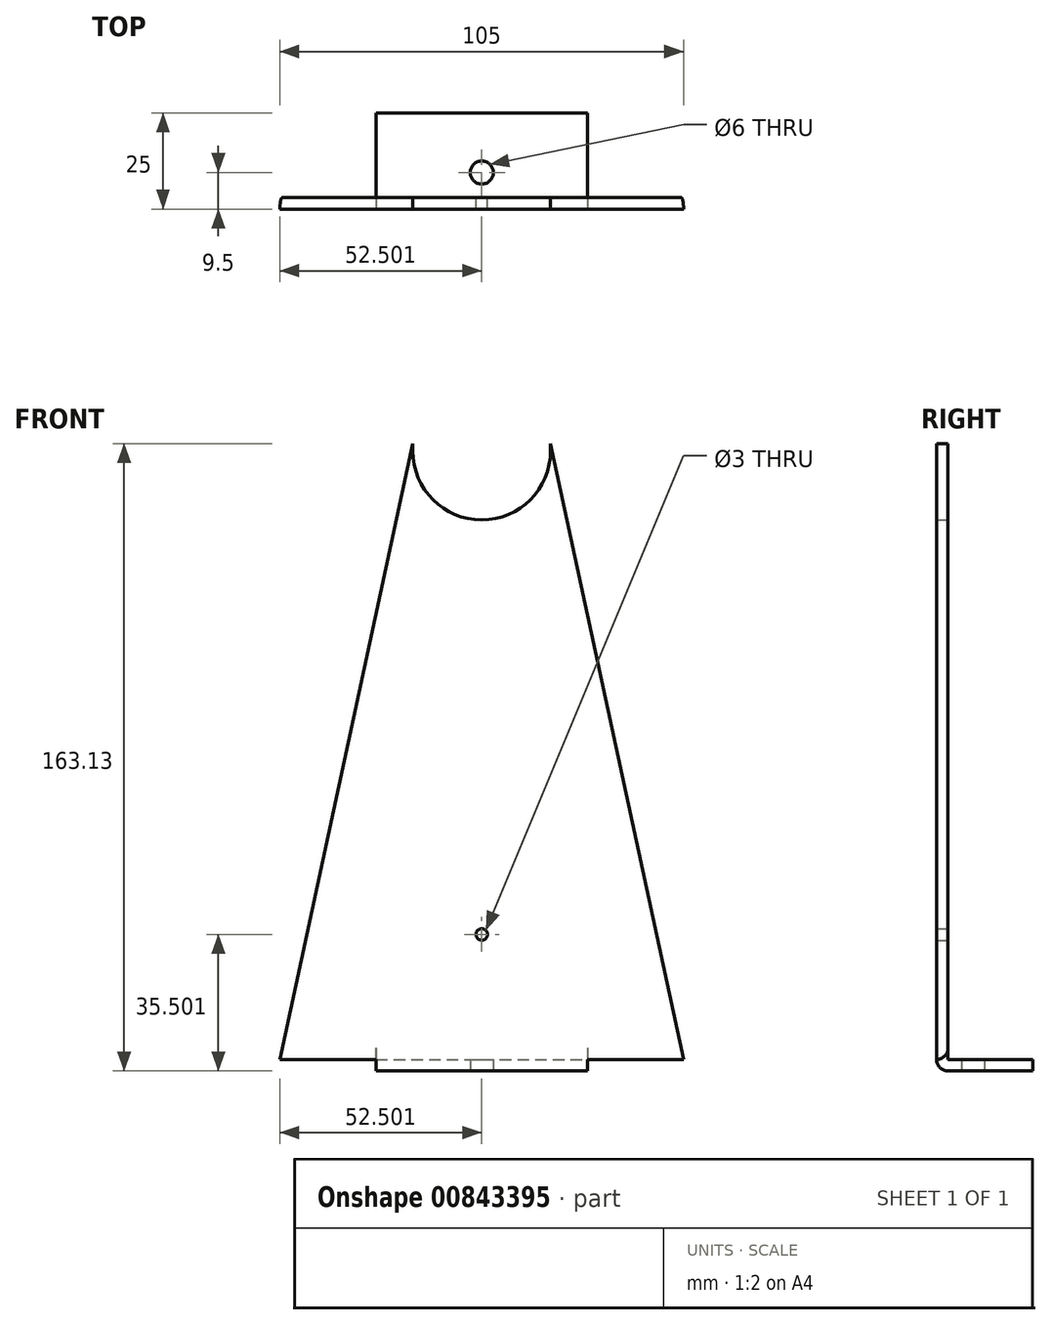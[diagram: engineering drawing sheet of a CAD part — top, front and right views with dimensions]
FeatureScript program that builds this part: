
annotation { "Feature Type Name" : "Feature", "Feature Type Description" : "" }
export const myFeature = defineFeature(function(context is Context, id is Id, definition is map)
    precondition{}
    {
        {
            var Q0;
            Q0=qCreatedBy(makeId("Front.planeOp"),FACE);
            var sketch = newSketch(context, id + "F0", { "sketchPlane" : qUnion([Q0])});
            skCircle(sketch, "E0", {"center": v(1053.9, -134.2) * mm, "radius": 17 * mm, "construction": true});
            skLineSegment(sketch, "E1", {"start": v(1680.14, -90.33) * mm, "end": v(1488.5, 408.9) * mm, "construction": true});
            skCircle(sketch, "E2", {"center": v(1053.9, -134.2) * mm, "radius": 21.5 * mm, "construction": true});
            skLineSegment(sketch, "E3", {"start": v(600.85, -74.2) * mm, "end": v(1722.15, -74.2) * mm, "construction": true});
            skLineSegment(sketch, "E4", {"start": v(549.42, 30.42) * mm, "end": v(557.61, 24.68) * mm, "construction": true});
            skLineSegment(sketch, "E5", {"start": v(556.15, 25.16) * mm, "end": v(512.34, -39.07) * mm, "construction": true});
            skLineSegment(sketch, "E6", {"start": v(553.17, 27) * mm, "end": v(509.45, -37.1) * mm, "construction": true});
            skLineSegment(sketch, "E7", {"start": v(550.2, 28.85) * mm, "end": v(506.56, -35.12) * mm, "construction": true});
            skLineSegment(sketch, "E8", {"start": v(506.6, -35.05) * mm, "end": v(512.39, -39) * mm, "construction": true});
            skLineSegment(sketch, "E9", {"start": v(570.93, 38.38) * mm, "end": v(557.61, 24.68) * mm, "construction": true});
            skLineSegment(sketch, "E10", {"start": v(552.29, 40.23) * mm, "end": v(549.42, 30.42) * mm, "construction": true});
            skLineSegment(sketch, "E11", {"start": v(600.85, -74.2) * mm, "end": v(440.53, 35.16) * mm, "construction": true});
            skLineSegment(sketch, "E12", {"start": v(713.05, 305.42) * mm, "end": v(656.4, 344.07) * mm, "construction": true});
            skLineSegment(sketch, "E13", {"start": v(702.52, 301.1) * mm, "end": v(656.02, 332.82) * mm, "construction": true});
            skLineSegment(sketch, "E14", {"start": v(710.06, 318.96) * mm, "end": v(669.92, 346.34) * mm, "construction": true});
            skLineSegment(sketch, "E15", {"start": v(689.46, 276.92) * mm, "end": v(655.21, 300.28) * mm, "construction": true});
            skLineSegment(sketch, "E16", {"start": v(615.02, -14.4) * mm, "end": v(402.92, 130.27) * mm, "construction": true});
            skLineSegment(sketch, "E17", {"start": v(559.84, 45.15) * mm, "end": v(550.25, 28.9) * mm, "construction": true});
            skLineSegment(sketch, "E18", {"start": v(562.86, 43.37) * mm, "end": v(553.2, 26.99) * mm, "construction": true});
            skLineSegment(sketch, "E19", {"start": v(565.87, 41.59) * mm, "end": v(556.13, 25.08) * mm, "construction": true});
            skLineSegment(sketch, "E20", {"start": v(565.87, 41.59) * mm, "end": v(559.84, 45.15) * mm, "construction": true});
            skLineSegment(sketch, "E21", {"start": v(472.04, 13.66) * mm, "end": v(769.02, 448.32) * mm, "construction": true});
            skArc(sketch, "E22", {"start": v(1006.96, -304.39) * mm, "mid": v(1011.65, -296.38) * mm, "end": v(1009.48, -287.35) * mm, "construction": true});
            skLineSegment(sketch, "E23", {"start": v(1053.9, -134.2) * mm, "end": v(1026.77, -317.41) * mm, "construction": true});
            skLineSegment(sketch, "E24", {"start": v(919.77, -241.35) * mm, "end": v(912.74, -288.83) * mm, "construction": true});
            skLineSegment(sketch, "E25", {"start": v(652.5, -164.98) * mm, "end": v(650.65, -171.73) * mm, "construction": true});
            skLineSegment(sketch, "E26", {"start": v(1031.93, -282.2) * mm, "end": v(579.95, -215.37) * mm, "construction": true});
            skLineSegment(sketch, "E27", {"start": v(674.61, -285.96) * mm, "end": v(640.98, -281) * mm, "construction": true});
            skLineSegment(sketch, "E28", {"start": v(675.34, -281.02) * mm, "end": v(641.71, -276.04) * mm, "construction": true});
            skLineSegment(sketch, "E29", {"start": v(1058.23, -251.72) * mm, "end": v(1048.27, -318.98) * mm, "construction": true});
            skLineSegment(sketch, "E30", {"start": v(945.2, -240.52) * mm, "end": v(983.81, -252.86) * mm, "construction": true});
            skLineSegment(sketch, "E31", {"start": v(941.1, -296.9) * mm, "end": v(949.25, -241.81) * mm, "construction": true});
            skLineSegment(sketch, "E32", {"start": v(941.66, -296.89) * mm, "end": v(949.79, -241.98) * mm, "construction": true});
            skLineSegment(sketch, "E33", {"start": v(973.82, -296.4) * mm, "end": v(980.43, -251.78) * mm, "construction": true});
            skLineSegment(sketch, "E34", {"start": v(972.56, -296.41) * mm, "end": v(979.23, -251.4) * mm, "construction": true});
            skLineSegment(sketch, "E35", {"start": v(964.98, -243.46) * mm, "end": v(956.63, -299.87) * mm, "construction": true});
            skLineSegment(sketch, "E36", {"start": v(983.81, -252.86) * mm, "end": v(977.37, -296.34) * mm, "construction": true});
            skLineSegment(sketch, "E37", {"start": v(945.2, -240.52) * mm, "end": v(936.84, -296.96) * mm, "construction": true});
            skLineSegment(sketch, "E38", {"start": v(979.95, -251.62) * mm, "end": v(973.32, -296.4) * mm, "construction": true});
            skLineSegment(sketch, "E39", {"start": v(949.06, -241.75) * mm, "end": v(940.9, -296.9) * mm, "construction": true});
            skLineSegment(sketch, "E40", {"start": v(940.66, -271.21) * mm, "end": v(945.36, -271.9) * mm, "construction": true});
            skLineSegment(sketch, "E41", {"start": v(944.62, -276.85) * mm, "end": v(939.93, -276.16) * mm, "construction": true});
            skLineSegment(sketch, "E42", {"start": v(946.27, -261.93) * mm, "end": v(942.12, -261.32) * mm, "construction": true});
            skLineSegment(sketch, "E43", {"start": v(940.8, -270.22) * mm, "end": v(945.5, -270.92) * mm, "construction": true});
            skLineSegment(sketch, "E44", {"start": v(941.39, -266.26) * mm, "end": v(946.09, -266.96) * mm, "construction": true});
            skLineSegment(sketch, "E45", {"start": v(941.24, -267.25) * mm, "end": v(945.94, -267.95) * mm, "construction": true});
            skArc(sketch, "E46", {"start": v(960.04, -276.86) * mm, "mid": v(966, -272.44) * mm, "end": v(961.58, -266.47) * mm, "construction": true});
            skArc(sketch, "E47", {"start": v(961.58, -266.47) * mm, "mid": v(955.61, -270.9) * mm, "end": v(960.04, -276.86) * mm, "construction": true});
            skLineSegment(sketch, "E48", {"start": v(1015.7, -245.42) * mm, "end": v(1005.73, -312.69) * mm, "construction": true});
            skLineSegment(sketch, "E49", {"start": v(1048.27, -318.98) * mm, "end": v(1005.73, -312.69) * mm, "construction": true});
            skLineSegment(sketch, "E50", {"start": v(1058.23, -251.72) * mm, "end": v(1015.7, -245.42) * mm, "construction": true});
            skArc(sketch, "E51", {"start": v(1011.94, -270.77) * mm, "mid": v(1016.63, -262.76) * mm, "end": v(1014.46, -253.73) * mm, "construction": true});
            skLineSegment(sketch, "E52", {"start": v(1037.98, -241.64) * mm, "end": v(948.95, -228.46) * mm, "construction": true});
            skLineSegment(sketch, "E53", {"start": v(576.43, -151.16) * mm, "end": v(632.5, -159.46) * mm, "construction": true});
            skLineSegment(sketch, "E54", {"start": v(575.4, -158.08) * mm, "end": v(631.06, -166.32) * mm, "construction": true});
            skLineSegment(sketch, "E55", {"start": v(575.3, -152) * mm, "end": v(574.56, -156.95) * mm, "construction": true});
            skArc(sketch, "E56", {"start": v(574.56, -156.95) * mm, "mid": v(574.75, -157.7) * mm, "end": v(575.4, -158.08) * mm, "construction": true});
            skArc(sketch, "E57", {"start": v(576.43, -151.16) * mm, "mid": v(575.69, -151.35) * mm, "end": v(575.3, -152) * mm, "construction": true});
            skLineSegment(sketch, "E58", {"start": v(631.06, -166.32) * mm, "end": v(650.65, -171.73) * mm, "construction": true});
            skLineSegment(sketch, "E59", {"start": v(632.5, -159.46) * mm, "end": v(652.5, -164.98) * mm, "construction": true});
            skLineSegment(sketch, "E60", {"start": v(600.85, -74.2) * mm, "end": v(567.5, -299.5) * mm, "construction": true});
            skLineSegment(sketch, "E61", {"start": v(644.77, -80.7) * mm, "end": v(612.1, -301.34) * mm, "construction": true});
            skLineSegment(sketch, "E62", {"start": v(641.71, -276.04) * mm, "end": v(640.98, -281) * mm, "construction": true});
            skLineSegment(sketch, "E63", {"start": v(675.34, -281.02) * mm, "end": v(674.61, -285.96) * mm, "construction": true});
            skLineSegment(sketch, "E64", {"start": v(607.36, -8.75) * mm, "end": v(864.68, 368.48) * mm, "construction": true});
            skLineSegment(sketch, "E65", {"start": v(622.48, -20.32) * mm, "end": v(871.92, 345.36) * mm, "construction": true});
            skLineSegment(sketch, "E66", {"start": v(615.02, -14.4) * mm, "end": v(879.24, 372.95) * mm, "construction": true});
            skLineSegment(sketch, "E67", {"start": v(1053.9, -134.2) * mm, "end": v(865.03, 414.2) * mm, "construction": true});
            skLineSegment(sketch, "E68", {"start": v(1034.15, -125.7) * mm, "end": v(850, 409.01) * mm, "construction": true});
            skLineSegment(sketch, "E69", {"start": v(861.66, 381.3) * mm, "end": v(851.9, 409.67) * mm, "construction": true});
            skLineSegment(sketch, "E70", {"start": v(1064.21, -115.34) * mm, "end": v(880.07, 419.37) * mm, "construction": true});
            skLineSegment(sketch, "E71", {"start": v(1053.9, -134.2) * mm, "end": v(645.8, -73.78) * mm, "construction": true});
            skLineSegment(sketch, "E72", {"start": v(743.09, -99.4) * mm, "end": v(644.17, -84.76) * mm, "construction": true});
            skLineSegment(sketch, "E73", {"start": v(746.34, -77.44) * mm, "end": v(647.42, -62.8) * mm, "construction": true});
            skLineSegment(sketch, "E74", {"start": v(1035.36, -145.1) * mm, "end": v(841.66, -116.43) * mm, "construction": true});
            skLineSegment(sketch, "E75", {"start": v(1039.32, -118.4) * mm, "end": v(845.61, -89.72) * mm, "construction": true});
            skLineSegment(sketch, "E76", {"start": v(879.24, 372.95) * mm, "end": v(768.93, 448.19) * mm, "construction": true});
            skLineSegment(sketch, "E77", {"start": v(966.15, -134.86) * mm, "end": v(995.58, -139.21) * mm, "construction": true});
            skLineSegment(sketch, "E78", {"start": v(960.23, -139.03) * mm, "end": v(994.85, -144.16) * mm, "construction": true});
            skLineSegment(sketch, "E79", {"start": v(963.6, -143.58) * mm, "end": v(964.04, -140.6) * mm, "construction": true});
            skArc(sketch, "E80", {"start": v(959.64, -143) * mm, "mid": v(959.83, -143.73) * mm, "end": v(960.48, -144.13) * mm, "construction": true});
            skLineSegment(sketch, "E81", {"start": v(960.48, -144.13) * mm, "end": v(962.46, -144.42) * mm, "construction": true});
            skArc(sketch, "E82", {"start": v(962.46, -144.42) * mm, "mid": v(963.2, -144.23) * mm, "end": v(963.6, -143.58) * mm, "construction": true});
            skLineSegment(sketch, "E83", {"start": v(965.3, -133.72) * mm, "end": v(967.21, -120.86) * mm, "construction": true});
            skLineSegment(sketch, "E84", {"start": v(963, -120.24) * mm, "end": v(959.64, -143) * mm, "construction": true});
            skLineSegment(sketch, "E85", {"start": v(962.42, -124.2) * mm, "end": v(966.63, -124.82) * mm, "construction": true});
            skArc(sketch, "E86", {"start": v(965.17, -139.77) * mm, "mid": v(964.43, -139.95) * mm, "end": v(964.04, -140.6) * mm, "construction": true});
            skLineSegment(sketch, "E87", {"start": v(961.7, -129.14) * mm, "end": v(965.9, -129.76) * mm, "construction": true});
            skLineSegment(sketch, "E88", {"start": v(960.08, -126.38) * mm, "end": v(968.24, -127.58) * mm, "construction": true});
            skLineSegment(sketch, "E89", {"start": v(974.82, -141.2) * mm, "end": v(975.55, -136.25) * mm, "construction": true});
            skArc(sketch, "E90", {"start": v(965.3, -133.72) * mm, "mid": v(965.5, -134.46) * mm, "end": v(966.15, -134.86) * mm, "construction": true});
            skLineSegment(sketch, "E91", {"start": v(964.14, -119.4) * mm, "end": v(966.37, -119.73) * mm, "construction": true});
            skArc(sketch, "E92", {"start": v(964.14, -119.4) * mm, "mid": v(963.4, -119.58) * mm, "end": v(963, -120.24) * mm, "construction": true});
            skArc(sketch, "E93", {"start": v(967.21, -120.86) * mm, "mid": v(967.03, -120.12) * mm, "end": v(966.37, -119.73) * mm, "construction": true});
            skLineSegment(sketch, "E94", {"start": v(995.58, -139.21) * mm, "end": v(999.8, -144.9) * mm, "construction": true});
            skLineSegment(sketch, "E95", {"start": v(979.72, -143.94) * mm, "end": v(981.04, -135.04) * mm, "construction": true});
            skArc(sketch, "E96", {"start": v(995.7, -145.3) * mm, "mid": v(995.5, -144.55) * mm, "end": v(994.85, -144.16) * mm, "construction": true});
            skArc(sketch, "E97", {"start": v(995.25, -148.26) * mm, "mid": v(995.44, -149) * mm, "end": v(996.1, -149.4) * mm, "construction": true});
            skArc(sketch, "E98", {"start": v(998.07, -149.7) * mm, "mid": v(998.82, -149.5) * mm, "end": v(999.2, -148.85) * mm, "construction": true});
            skLineSegment(sketch, "E99", {"start": v(996.1, -149.4) * mm, "end": v(998.07, -149.7) * mm, "construction": true});
            skLineSegment(sketch, "E100", {"start": v(999.2, -148.85) * mm, "end": v(999.8, -144.9) * mm, "construction": true});
            skLineSegment(sketch, "E101", {"start": v(995.25, -148.26) * mm, "end": v(995.7, -145.3) * mm, "construction": true});
            skLineSegment(sketch, "E102", {"start": v(985.2, -142.73) * mm, "end": v(985.94, -137.79) * mm, "construction": true});
            skLineSegment(sketch, "E103", {"start": v(995.47, -146.78) * mm, "end": v(993.6, -159.38) * mm, "construction": true});
            skEllipticalArc(sketch, "E104", {"construction": true});
            skLineSegment(sketch, "E105", {"start": v(850, 409.01) * mm, "end": v(880.07, 419.37) * mm, "construction": true});
            skLineSegment(sketch, "E106", {"start": v(859.77, 380.65) * mm, "end": v(861.66, 381.3) * mm, "construction": true});
            skLineSegment(sketch, "E107", {"start": v(1053.92, -134.2) * mm, "end": v(1520.05, 326.73) * mm, "construction": true});
            skLineSegment(sketch, "E108", {"start": v(1075.4, -135.33) * mm, "end": v(1510.36, 294.78) * mm, "construction": true});
            skLineSegment(sketch, "E109", {"start": v(1060.7, -105.14) * mm, "end": v(1497.91, 327.2) * mm, "construction": true});
            skLineSegment(sketch, "E110", {"start": v(879.24, 372.95) * mm, "end": v(1502.3, 372.95) * mm, "construction": true});
            skLineSegment(sketch, "E111", {"start": v(901.53, 357.05) * mm, "end": v(1486.45, 357.05) * mm, "construction": true});
            skLineSegment(sketch, "E112", {"start": v(890.58, 388.85) * mm, "end": v(1474.25, 388.85) * mm, "construction": true});
            skArc(sketch, "E113", {"start": v(1486.5, 356.93) * mm, "mid": v(1487.54, 375.64) * mm, "end": v(1474.25, 388.85) * mm, "construction": true});
            skArc(sketch, "E114", {"start": v(890.58, 388.85) * mm, "mid": v(888.92, 370.5) * mm, "end": v(901.53, 357.05) * mm, "construction": true});
            skArc(sketch, "E115", {"start": v(1510.36, 294.78) * mm, "mid": v(1511.76, 313.92) * mm, "end": v(1497.91, 327.2) * mm, "construction": true});
            skLineSegment(sketch, "E116", {"start": v(1722.15, -74.2) * mm, "end": v(1680.14, -90.33) * mm, "construction": true});
            skLineSegment(sketch, "E117", {"start": v(915.6, -231.4) * mm, "end": v(630.6, -162.69) * mm, "construction": true});
            skLineSegment(sketch, "E118", {"start": v(913.6, -239.65) * mm, "end": v(801.39, -212.6) * mm, "construction": true});
            skLineSegment(sketch, "E119", {"start": v(917.6, -223.13) * mm, "end": v(805.37, -196.07) * mm, "construction": true});
            skArc(sketch, "E120", {"start": v(924, -233.74) * mm, "mid": v(919.82, -232.5) * mm, "end": v(915.6, -231.4) * mm, "construction": true});
            skArc(sketch, "E121", {"start": v(921.8, -241.96) * mm, "mid": v(917.73, -240.73) * mm, "end": v(913.6, -239.65) * mm, "construction": true});
            skArc(sketch, "E122", {"start": v(919.09, -223.5) * mm, "mid": v(918.34, -223.31) * mm, "end": v(917.6, -223.13) * mm, "construction": true});
            skLineSegment(sketch, "E123", {"start": v(631.26, -168.55) * mm, "end": v(633.85, -157.83) * mm, "construction": true});
            skLineSegment(sketch, "E124", {"start": v(1013.2, -262.25) * mm, "end": v(924, -233.74) * mm, "construction": true});
            skLineSegment(sketch, "E125", {"start": v(1011.94, -270.77) * mm, "end": v(921.42, -241.84) * mm, "construction": true});
            skLineSegment(sketch, "E126", {"start": v(1014.46, -253.73) * mm, "end": v(985.84, -244.58) * mm, "construction": true});
            skLineSegment(sketch, "E127", {"start": v(631.26, -168.55) * mm, "end": v(641.06, -174.4) * mm, "construction": true});
            skLineSegment(sketch, "E128", {"start": v(633.85, -157.83) * mm, "end": v(651.56, -156.6) * mm, "construction": true});
            skLineSegment(sketch, "E129", {"start": v(805.37, -196.07) * mm, "end": v(651.56, -156.6) * mm, "construction": true});
            skLineSegment(sketch, "E130", {"start": v(693.7, -188.3) * mm, "end": v(801.39, -212.6) * mm, "construction": true});
            skLineSegment(sketch, "E131", {"start": v(641.06, -174.4) * mm, "end": v(688.9, -185.2) * mm, "construction": true});
            skArc(sketch, "E132", {"start": v(905.87, -297.16) * mm, "mid": v(910.24, -297.33) * mm, "end": v(914.6, -297.34) * mm, "construction": true});
            skArc(sketch, "E133", {"start": v(906.36, -288.67) * mm, "mid": v(910.61, -288.83) * mm, "end": v(914.87, -288.83) * mm, "construction": true});
            skArc(sketch, "E134", {"start": v(905.39, -305.65) * mm, "mid": v(910.06, -305.83) * mm, "end": v(914.73, -305.84) * mm, "construction": true});
            skLineSegment(sketch, "E135", {"start": v(1008.18, -295.87) * mm, "end": v(914.6, -297.34) * mm, "construction": true});
            skLineSegment(sketch, "E136", {"start": v(1009.48, -287.35) * mm, "end": v(914.47, -288.84) * mm, "construction": true});
            skLineSegment(sketch, "E137", {"start": v(1006.96, -304.39) * mm, "end": v(914.73, -305.84) * mm, "construction": true});
            skLineSegment(sketch, "E138", {"start": v(688.9, -185.2) * mm, "end": v(693.7, -188.3) * mm, "construction": true});
            skArc(sketch, "E139", {"start": v(919.09, -223.5) * mm, "mid": v(951.5, -237.06) * mm, "end": v(985.84, -244.58) * mm, "construction": true});
            skLineSegment(sketch, "E140", {"start": v(936.85, -296.96) * mm, "end": v(977.38, -296.34) * mm, "construction": true});
            skFitSpline(sketch, "E141", {"points": [v(872.4, 346.08) * mm, v(876.18, 356.24) * mm, v(881.69, 371.02) * mm, v(868.73, 369.09) * mm, v(864.68, 368.48) * mm], "construction": true});
            skLineSegment(sketch, "E142", {"start": v(662.14, -86.28) * mm, "end": v(644.63, -83.68) * mm, "construction": true});
            skLineSegment(sketch, "E143", {"start": v(665.07, -66.5) * mm, "end": v(647.56, -63.9) * mm, "construction": true});
            skLineSegment(sketch, "E144", {"start": v(664.41, -84.6) * mm, "end": v(666.76, -68.76) * mm, "construction": true});
            skArc(sketch, "E145", {"start": v(662.14, -86.28) * mm, "mid": v(663.62, -85.9) * mm, "end": v(664.41, -84.6) * mm, "construction": true});
            skArc(sketch, "E146", {"start": v(666.76, -68.76) * mm, "mid": v(666.38, -67.28) * mm, "end": v(665.07, -66.5) * mm, "construction": true});
            skArc(sketch, "E147", {"start": v(591.11, -61.72) * mm, "mid": v(584.1, -63.16) * mm, "end": v(585.54, -70.17) * mm, "construction": true});
            skLineSegment(sketch, "E148", {"start": v(585.54, -70.17) * mm, "end": v(605.08, -83.05) * mm, "construction": true});
            skLineSegment(sketch, "E149", {"start": v(601.2, -91.02) * mm, "end": v(582.02, -84.5) * mm, "construction": true});
            skLineSegment(sketch, "E150", {"start": v(584.15, -63.19) * mm, "end": v(613.37, -82.46) * mm, "construction": true});
            skLineSegment(sketch, "E151", {"start": v(607.46, -8.63) * mm, "end": v(572.75, -54.03) * mm, "construction": true});
            skLineSegment(sketch, "E152", {"start": v(644.18, -84.66) * mm, "end": v(644.29, -83.94) * mm, "construction": true});
            skLineSegment(sketch, "E153", {"start": v(591.11, -61.72) * mm, "end": v(618.65, -79.88) * mm, "construction": true});
            skArc(sketch, "E154", {"start": v(618.65, -79.88) * mm, "mid": v(620.57, -80.9) * mm, "end": v(622.66, -81.47) * mm, "construction": true});
            skLineSegment(sketch, "E155", {"start": v(644.18, -84.66) * mm, "end": v(622.66, -81.47) * mm, "construction": true});
            skArc(sketch, "E156", {"start": v(644.63, -83.68) * mm, "mid": v(644.4, -83.74) * mm, "end": v(644.29, -83.94) * mm, "construction": true});
            skLineSegment(sketch, "E157", {"start": v(644.18, -84.66) * mm, "end": v(644.19, -84.63) * mm, "construction": true});
            skArc(sketch, "E158", {"start": v(601.2, -91.02) * mm, "mid": v(606.49, -88.67) * mm, "end": v(605.08, -83.05) * mm, "construction": true});
            skArc(sketch, "E159", {"start": v(617.78, -52.64) * mm, "mid": v(628.06, -58.54) * mm, "end": v(639.47, -61.73) * mm, "construction": true});
            skLineSegment(sketch, "E160", {"start": v(670.48, -77.43) * mm, "end": v(577.33, -63.64) * mm, "construction": true});
            skLineSegment(sketch, "E161", {"start": v(647.4, -62.9) * mm, "end": v(639.47, -61.73) * mm, "construction": true});
            skArc(sketch, "E162", {"start": v(647.3, -63.56) * mm, "mid": v(647.36, -63.78) * mm, "end": v(647.56, -63.9) * mm, "construction": true});
            skLineSegment(sketch, "E163", {"start": v(647.3, -63.56) * mm, "end": v(647.4, -62.9) * mm, "construction": true});
            skArc(sketch, "E164", {"start": v(614, -32.51) * mm, "mid": v(611.92, -43.32) * mm, "end": v(617.78, -52.64) * mm, "construction": true});
            skLineSegment(sketch, "E165", {"start": v(614, -32.51) * mm, "end": v(622.56, -20.17) * mm, "construction": true});
            skLineSegment(sketch, "E166", {"start": v(577.33, -63.64) * mm, "end": v(629.71, 4.8) * mm, "construction": true});
            skArc(sketch, "E167", {"start": v(598.7, -25.94) * mm, "mid": v(602.23, -29.14) * mm, "end": v(601.27, -24.48) * mm, "construction": true});
            skArc(sketch, "E168", {"start": v(572.75, -54.03) * mm, "mid": v(569.56, -71.65) * mm, "end": v(582.02, -84.5) * mm, "construction": true});
            skCircle(sketch, "E169", {"center": v(586.41, -46.03) * mm, "radius": 2 * mm, "construction": true});
            skArc(sketch, "E170", {"start": v(585.71, -43.63) * mm, "mid": v(585.82, -48.46) * mm, "end": v(588.14, -44.23) * mm, "construction": true});
            skArc(sketch, "E171", {"start": v(632.31, -4.97) * mm, "mid": v(632.7, -3.49) * mm, "end": v(631.94, -2.16) * mm, "construction": true});
            skLineSegment(sketch, "E172", {"start": v(608.84, -9.3) * mm, "end": v(619.6, 4.75) * mm, "construction": true});
            skLineSegment(sketch, "E173", {"start": v(621.55, -19.02) * mm, "end": v(632.31, -4.97) * mm, "construction": true});
            skLineSegment(sketch, "E174", {"start": v(607.46, -8.63) * mm, "end": v(608.42, -9.36) * mm, "construction": true});
            skArc(sketch, "E175", {"start": v(621.55, -19.02) * mm, "mid": v(621.5, -19.24) * mm, "end": v(621.6, -19.44) * mm, "construction": true});
            skLineSegment(sketch, "E176", {"start": v(621.6, -19.44) * mm, "end": v(622.56, -20.17) * mm, "construction": true});
            skCircle(sketch, "E177", {"center": v(601, -26.97) * mm, "radius": 2 * mm, "construction": true});
            skArc(sketch, "E178", {"start": v(608.42, -9.36) * mm, "mid": v(608.64, -9.42) * mm, "end": v(608.84, -9.3) * mm, "construction": true});
            skLineSegment(sketch, "E179", {"start": v(608.42, -9.36) * mm, "end": v(607.46, -8.63) * mm, "construction": true});
            skArc(sketch, "E180", {"start": v(622.4, 5.12) * mm, "mid": v(620.93, 5.52) * mm, "end": v(619.6, 4.75) * mm, "construction": true});
            skLineSegment(sketch, "E181", {"start": v(631.94, -2.16) * mm, "end": v(622.4, 5.12) * mm, "construction": true});
            skLineSegment(sketch, "E182", {"start": v(619.71, -24.29) * mm, "end": v(604.42, -12.6) * mm, "construction": true});
            skLineSegment(sketch, "E183", {"start": v(639.24, -83.93) * mm, "end": v(642.46, -62.17) * mm, "construction": true});
            skCircle(sketch, "E184", {"center": v(600.85, -74.2) * mm, "radius": 5 * mm, "construction": true});
            skLineSegment(sketch, "E185", {"start": v(621.6, -19.44) * mm, "end": v(608.42, -9.36) * mm, "construction": true});
            skLineSegment(sketch, "E186", {"start": v(644.29, -83.94) * mm, "end": v(647.3, -63.56) * mm, "construction": true});
            skLineSegment(sketch, "E187", {"start": v(841.66, -116.43) * mm, "end": v(743.09, -99.4) * mm, "construction": true});
            skLineSegment(sketch, "E188", {"start": v(746.34, -77.44) * mm, "end": v(845.61, -89.72) * mm, "construction": true});
            skEllipse(sketch, "E189", {"center": v(843.64, -103.07) * mm, "majorRadius": 13.5 * mm, "minorRadius": 8.5 * mm, "majorAxis": v(-0.15, -0.99), "construction": true});
            skCircle(sketch, "E190", {"center": v(645.8, -73.78) * mm, "radius": 11 * mm, "construction": true});
            skLineSegment(sketch, "E191", {"start": v(634.82, -284.6) * mm, "end": v(635, -277.6) * mm, "construction": true});
            skLineSegment(sketch, "E192", {"start": v(558, -275.8) * mm, "end": v(614.08, -284.09) * mm, "construction": true});
            skLineSegment(sketch, "E193", {"start": v(559.02, -268.88) * mm, "end": v(614.68, -277.1) * mm, "construction": true});
            skLineSegment(sketch, "E194", {"start": v(557.16, -274.67) * mm, "end": v(557.89, -269.73) * mm, "construction": true});
            skArc(sketch, "E195", {"start": v(559.02, -268.88) * mm, "mid": v(558.28, -269.07) * mm, "end": v(557.89, -269.73) * mm, "construction": true});
            skArc(sketch, "E196", {"start": v(557.16, -274.67) * mm, "mid": v(557.34, -275.42) * mm, "end": v(558, -275.8) * mm, "construction": true});
            skLineSegment(sketch, "E197", {"start": v(614.68, -277.1) * mm, "end": v(635, -277.6) * mm, "construction": true});
            skLineSegment(sketch, "E198", {"start": v(614.08, -284.09) * mm, "end": v(634.82, -284.6) * mm, "construction": true});
            skLineSegment(sketch, "E199", {"start": v(905.87, -297.16) * mm, "end": v(613.19, -280.45) * mm, "construction": true});
            skLineSegment(sketch, "E200", {"start": v(906.36, -288.67) * mm, "end": v(791.11, -282.1) * mm, "construction": true});
            skLineSegment(sketch, "E201", {"start": v(905.39, -305.65) * mm, "end": v(790.14, -299.07) * mm, "construction": true});
            skLineSegment(sketch, "E202", {"start": v(615.52, -275.03) * mm, "end": v(614.89, -286.04) * mm, "construction": true});
            skLineSegment(sketch, "E203", {"start": v(615.52, -275.03) * mm, "end": v(632.73, -270.73) * mm, "construction": true});
            skLineSegment(sketch, "E204", {"start": v(614.89, -286.04) * mm, "end": v(631.5, -292.34) * mm, "construction": true});
            skLineSegment(sketch, "E205", {"start": v(790.14, -299.07) * mm, "end": v(631.5, -292.34) * mm, "construction": true});
            skLineSegment(sketch, "E206", {"start": v(632.73, -270.73) * mm, "end": v(791.11, -282.1) * mm, "construction": true});
            skLineSegment(sketch, "E207", {"start": v(703.93, 282.77) * mm, "end": v(553.52, 27.55) * mm, "construction": true});
            skArc(sketch, "E208", {"start": v(703.93, 282.77) * mm, "mid": v(707.75, 289.77) * mm, "end": v(711.1, 297.02) * mm, "construction": true});
            skArc(sketch, "E209", {"start": v(695.75, 287.6) * mm, "mid": v(699.27, 294.04) * mm, "end": v(702.35, 300.71) * mm, "construction": true});
            skArc(sketch, "E210", {"start": v(712.12, 277.95) * mm, "mid": v(716.24, 285.5) * mm, "end": v(719.85, 293.32) * mm, "construction": true});
            skLineSegment(sketch, "E211", {"start": v(712.12, 277.95) * mm, "end": v(570.93, 38.38) * mm, "construction": true});
            skLineSegment(sketch, "E212", {"start": v(695.75, 287.6) * mm, "end": v(578.7, 88.99) * mm, "construction": true});
            skLineSegment(sketch, "E213", {"start": v(577.7, 83.34) * mm, "end": v(552.29, 40.23) * mm, "construction": true});
            skLineSegment(sketch, "E214", {"start": v(764.21, 422.8) * mm, "end": v(711.1, 297.02) * mm, "construction": true});
            skLineSegment(sketch, "E215", {"start": v(781.6, 439.55) * mm, "end": v(719.85, 293.32) * mm, "construction": true});
            skLineSegment(sketch, "E216", {"start": v(758.12, 432.79) * mm, "end": v(702.35, 300.71) * mm, "construction": true});
            skLineSegment(sketch, "E217", {"start": v(452.18, 96.19) * mm, "end": v(408.28, 32.03) * mm, "construction": true});
            skLineSegment(sketch, "E218", {"start": v(454.99, 94.09) * mm, "end": v(411.17, 30.06) * mm, "construction": true});
            skLineSegment(sketch, "E219", {"start": v(457.79, 91.98) * mm, "end": v(414.05, 28.08) * mm, "construction": true});
            skLineSegment(sketch, "E220", {"start": v(414.1, 28.15) * mm, "end": v(408.33, 32.1) * mm, "construction": true});
            skLineSegment(sketch, "E221", {"start": v(577.7, 83.34) * mm, "end": v(578.7, 88.99) * mm, "construction": true});
            skCircle(sketch, "E222", {"center": v(795.03, 249.5) * mm, "radius": 9.5 * mm, "construction": true});
            skLineSegment(sketch, "E223", {"start": v(789.96, 238.43) * mm, "end": v(790.5, 237.46) * mm, "construction": true});
            skLineSegment(sketch, "E224", {"start": v(796.05, 242.82) * mm, "end": v(795.76, 244.37) * mm, "construction": true});
            skLineSegment(sketch, "E225", {"start": v(789.82, 248.52) * mm, "end": v(790.17, 248.58) * mm, "construction": true});
            skLineSegment(sketch, "E226", {"start": v(796.02, 244.3) * mm, "end": v(789.82, 248.52) * mm, "construction": true});
            skLineSegment(sketch, "E227", {"start": v(784, 242.2) * mm, "end": v(792.26, 236.56) * mm, "construction": true});
            skLineSegment(sketch, "E228", {"start": v(792.26, 236.56) * mm, "end": v(793.8, 238.84) * mm, "construction": true});
            skLineSegment(sketch, "E229", {"start": v(791.91, 236.5) * mm, "end": v(792.26, 236.56) * mm, "construction": true});
            skLineSegment(sketch, "E230", {"start": v(784.06, 241.85) * mm, "end": v(784, 242.2) * mm, "construction": true});
            skLineSegment(sketch, "E231", {"start": v(795.95, 244.64) * mm, "end": v(790.17, 248.58) * mm, "construction": true});
            skLineSegment(sketch, "E232", {"start": v(786.57, 240.74) * mm, "end": v(789.96, 238.43) * mm, "construction": true});
            skLineSegment(sketch, "E233", {"start": v(791.91, 236.5) * mm, "end": v(784.06, 241.85) * mm, "construction": true});
            skLineSegment(sketch, "E234", {"start": v(786.58, 243.77) * mm, "end": v(789.82, 248.52) * mm, "construction": true});
            skLineSegment(sketch, "E235", {"start": v(787.99, 239.18) * mm, "end": v(793.06, 246.61) * mm, "construction": true});
            skLineSegment(sketch, "E236", {"start": v(786.39, 240.48) * mm, "end": v(791.18, 247.5) * mm, "construction": true});
            skLineSegment(sketch, "E237", {"start": v(786.08, 240.81) * mm, "end": v(791, 248.02) * mm, "construction": true});
            skLineSegment(sketch, "E238", {"start": v(786.57, 240.74) * mm, "end": v(785.47, 240.9) * mm, "construction": true});
            skLineSegment(sketch, "E239", {"start": v(789.96, 238.43) * mm, "end": v(794.75, 245.46) * mm, "construction": true});
            skLineSegment(sketch, "E240", {"start": v(790.2, 238) * mm, "end": v(795.12, 245.2) * mm, "construction": true});
            skLineSegment(sketch, "E241", {"start": v(784, 242.2) * mm, "end": v(785.55, 244.47) * mm, "construction": true});
            skLineSegment(sketch, "E242", {"start": v(793.8, 238.84) * mm, "end": v(785.55, 244.47) * mm, "construction": true});
            skLineSegment(sketch, "E243", {"start": v(792.78, 239.54) * mm, "end": v(796.02, 244.3) * mm, "construction": true});
            skArc(sketch, "E244", {"start": v(962.06, -126.67) * mm, "mid": v(930.44, 82.62) * mm, "end": v(787.99, 239.18) * mm, "construction": true});
            skLineSegment(sketch, "E245", {"start": v(679.65, 313.68) * mm, "end": v(680.2, 312.7) * mm, "construction": true});
            skLineSegment(sketch, "E246", {"start": v(685.7, 319.54) * mm, "end": v(685.64, 319.88) * mm, "construction": true});
            skLineSegment(sketch, "E247", {"start": v(679.5, 323.76) * mm, "end": v(679.86, 323.83) * mm, "construction": true});
            skLineSegment(sketch, "E248", {"start": v(685.7, 319.54) * mm, "end": v(679.5, 323.76) * mm, "construction": true});
            skLineSegment(sketch, "E249", {"start": v(673.69, 317.44) * mm, "end": v(681.95, 311.8) * mm, "construction": true});
            skLineSegment(sketch, "E250", {"start": v(681.95, 311.8) * mm, "end": v(683.5, 314.08) * mm, "construction": true});
            skLineSegment(sketch, "E251", {"start": v(681.6, 311.74) * mm, "end": v(681.95, 311.8) * mm, "construction": true});
            skLineSegment(sketch, "E252", {"start": v(673.75, 317.1) * mm, "end": v(673.69, 317.44) * mm, "construction": true});
            skLineSegment(sketch, "E253", {"start": v(685.64, 319.88) * mm, "end": v(679.86, 323.83) * mm, "construction": true});
            skLineSegment(sketch, "E254", {"start": v(676.27, 315.99) * mm, "end": v(679.65, 313.68) * mm, "construction": true});
            skLineSegment(sketch, "E255", {"start": v(681.6, 311.74) * mm, "end": v(673.75, 317.1) * mm, "construction": true});
            skLineSegment(sketch, "E256", {"start": v(676.27, 319.01) * mm, "end": v(679.5, 323.76) * mm, "construction": true});
            skLineSegment(sketch, "E257", {"start": v(677.68, 314.42) * mm, "end": v(682.75, 321.86) * mm, "construction": true});
            skLineSegment(sketch, "E258", {"start": v(676.27, 315.99) * mm, "end": v(681.05, 323.01) * mm, "construction": true});
            skLineSegment(sketch, "E259", {"start": v(675.77, 316.06) * mm, "end": v(680.68, 323.26) * mm, "construction": true});
            skLineSegment(sketch, "E260", {"start": v(676.27, 315.99) * mm, "end": v(675.16, 316.14) * mm, "construction": true});
            skLineSegment(sketch, "E261", {"start": v(679.65, 313.68) * mm, "end": v(684.44, 320.7) * mm, "construction": true});
            skLineSegment(sketch, "E262", {"start": v(679.9, 313.24) * mm, "end": v(684.81, 320.45) * mm, "construction": true});
            skLineSegment(sketch, "E263", {"start": v(673.69, 317.44) * mm, "end": v(675.24, 319.72) * mm, "construction": true});
            skLineSegment(sketch, "E264", {"start": v(683.5, 314.08) * mm, "end": v(675.24, 319.72) * mm, "construction": true});
            skLineSegment(sketch, "E265", {"start": v(682.47, 314.79) * mm, "end": v(685.7, 319.54) * mm, "construction": true});
            skArc(sketch, "E266", {"start": v(702.52, 301.1) * mm, "mid": v(708.88, 308.94) * mm, "end": v(710.06, 318.96) * mm, "construction": true});
            skArc(sketch, "E267", {"start": v(669.92, 346.34) * mm, "mid": v(661, 341.6) * mm, "end": v(656.02, 332.82) * mm, "construction": true});
            skArc(sketch, "E268", {"start": v(699, -121.18) * mm, "mid": v(709.07, -114.4) * mm, "end": v(703.24, -103.77) * mm, "construction": true});
            skArc(sketch, "E269", {"start": v(666.37, -98.3) * mm, "mid": v(657.7, -106.8) * mm, "end": v(665.37, -116.2) * mm, "construction": true});
            skLineSegment(sketch, "E270", {"start": v(699, -121.18) * mm, "end": v(665.37, -116.2) * mm, "construction": true});
            skLineSegment(sketch, "E271", {"start": v(701.91, -101.58) * mm, "end": v(702.96, -94.48) * mm, "construction": true});
            skLineSegment(sketch, "E272", {"start": v(668.28, -96.6) * mm, "end": v(669.33, -89.5) * mm, "construction": true});
            skLineSegment(sketch, "E273", {"start": v(667.15, -104.24) * mm, "end": v(700.78, -109.21) * mm, "construction": true});
            skLineSegment(sketch, "E274", {"start": v(666.24, -110.37) * mm, "end": v(699.87, -115.35) * mm, "construction": true});
            skLineSegment(sketch, "E275", {"start": v(703.4, -112.74) * mm, "end": v(663.63, -106.85) * mm, "construction": true});
            skArc(sketch, "E276", {"start": v(667.15, -104.24) * mm, "mid": v(663.63, -106.85) * mm, "end": v(666.24, -110.37) * mm, "construction": true});
            skArc(sketch, "E277", {"start": v(666.37, -98.3) * mm, "mid": v(667.63, -97.8) * mm, "end": v(668.28, -96.6) * mm, "construction": true});
            skArc(sketch, "E278", {"start": v(699.87, -115.35) * mm, "mid": v(703.4, -112.74) * mm, "end": v(700.78, -109.21) * mm, "construction": true});
            skArc(sketch, "E279", {"start": v(701.91, -101.58) * mm, "mid": v(702.18, -102.91) * mm, "end": v(703.24, -103.77) * mm, "construction": true});
            skLineSegment(sketch, "E280", {"start": v(702.12, -93.34) * mm, "end": v(670.46, -88.65) * mm, "construction": true});
            skArc(sketch, "E281", {"start": v(670.46, -88.65) * mm, "mid": v(669.72, -88.84) * mm, "end": v(669.33, -89.5) * mm, "construction": true});
            skArc(sketch, "E282", {"start": v(702.96, -94.48) * mm, "mid": v(702.78, -93.73) * mm, "end": v(702.12, -93.34) * mm, "construction": true});
            skCircle(sketch, "E283", {"center": v(1054.53, -129.2) * mm, "radius": 89.9 * mm, "construction": true});
            skCircle(sketch, "E284", {"center": v(600.85, -74.2) * mm, "radius": 41.4 * mm, "construction": true});
            skLineSegment(sketch, "E285", {"start": v(1055.81, -39.3) * mm, "end": v(601.44, -32.8) * mm, "construction": true});
            skLineSegment(sketch, "E286", {"start": v(459.53, 91.84) * mm, "end": v(451.2, 97.38) * mm, "construction": true});
            skLineSegment(sketch, "E287", {"start": v(459.13, 114.77) * mm, "end": v(451.2, 97.38) * mm, "construction": true});
            skLineSegment(sketch, "E288", {"start": v(462.18, 93.88) * mm, "end": v(459.53, 91.84) * mm, "construction": true});
            skArc(sketch, "E289", {"start": v(462.18, 93.88) * mm, "mid": v(473.4, 103.7) * mm, "end": v(483.33, 114.82) * mm, "construction": true});
            skLineSegment(sketch, "E290", {"start": v(469.46, 106.9) * mm, "end": v(457.81, 92.06) * mm, "construction": true});
            skLineSegment(sketch, "E291", {"start": v(466.7, 109.06) * mm, "end": v(454.96, 94.1) * mm, "construction": true});
            skLineSegment(sketch, "E292", {"start": v(463.96, 111.22) * mm, "end": v(452.12, 96.14) * mm, "construction": true});
            skLineSegment(sketch, "E293", {"start": v(463.96, 111.22) * mm, "end": v(469.46, 106.9) * mm, "construction": true});
            skLineSegment(sketch, "E294", {"start": v(638.46, 327.51) * mm, "end": v(455.36, 94.61) * mm, "construction": true});
            skArc(sketch, "E295", {"start": v(649.12, 339.36) * mm, "mid": v(643.6, 333.61) * mm, "end": v(638.46, 327.51) * mm, "construction": true});
            skArc(sketch, "E296", {"start": v(655.75, 332.55) * mm, "mid": v(650.65, 327.26) * mm, "end": v(645.92, 321.64) * mm, "construction": true});
            skArc(sketch, "E297", {"start": v(637.86, 341.42) * mm, "mid": v(634.34, 337.47) * mm, "end": v(630.99, 333.38) * mm, "construction": true});
            skLineSegment(sketch, "E298", {"start": v(630.99, 333.38) * mm, "end": v(459.13, 114.77) * mm, "construction": true});
            skLineSegment(sketch, "E299", {"start": v(645.92, 321.64) * mm, "end": v(483.33, 114.82) * mm, "construction": true});
            skLineSegment(sketch, "E300", {"start": v(746.99, 434.56) * mm, "end": v(649.12, 339.36) * mm, "construction": true});
            skLineSegment(sketch, "E301", {"start": v(756.26, 456.83) * mm, "end": v(636.32, 340.16) * mm, "construction": true});
            skLineSegment(sketch, "E302", {"start": v(758.51, 432.52) * mm, "end": v(655.75, 332.55) * mm, "construction": true});
            skLineSegment(sketch, "E303", {"start": v(1469.36, 401.56) * mm, "end": v(1507.64, 416.26) * mm, "construction": true});
            skLineSegment(sketch, "E304", {"start": v(1507.64, 416.26) * mm, "end": v(1552.44, 299.56) * mm, "construction": true});
            skLineSegment(sketch, "E305", {"start": v(1552.44, 299.56) * mm, "end": v(1514.16, 284.87) * mm, "construction": true});
            skLineSegment(sketch, "E306", {"start": v(1514.16, 284.87) * mm, "end": v(1469.36, 401.56) * mm, "construction": true});
            skLineSegment(sketch, "E307", {"start": v(844.6, 337.76) * mm, "end": v(883.44, 311.27) * mm, "construction": true});
            skLineSegment(sketch, "E308", {"start": v(844.6, 337.76) * mm, "end": v(836.16, 325.37) * mm, "construction": true});
            skLineSegment(sketch, "E309", {"start": v(836.16, 325.37) * mm, "end": v(874.98, 298.88) * mm, "construction": true});
            skLineSegment(sketch, "E310", {"start": v(874.98, 298.88) * mm, "end": v(883.44, 311.27) * mm, "construction": true});
            skLineSegment(sketch, "E311", {"start": v(864.68, 368.48) * mm, "end": v(778.96, 242.82) * mm, "construction": true});
            skLineSegment(sketch, "E312", {"start": v(864.68, 368.48) * mm, "end": v(862.2, 370.17) * mm, "construction": true});
            skLineSegment(sketch, "E313", {"start": v(862.2, 370.17) * mm, "end": v(776.49, 244.51) * mm, "construction": true});
            skLineSegment(sketch, "E314", {"start": v(776.49, 244.51) * mm, "end": v(778.96, 242.82) * mm, "construction": true});
            skLineSegment(sketch, "E315", {"start": v(853.45, 313.52) * mm, "end": v(871.62, 301.13) * mm, "construction": true});
            skLineSegment(sketch, "E316", {"start": v(853.45, 313.52) * mm, "end": v(798.8, 233.4) * mm, "construction": true});
            skLineSegment(sketch, "E317", {"start": v(798.8, 233.4) * mm, "end": v(816.96, 221) * mm, "construction": true});
            skLineSegment(sketch, "E318", {"start": v(816.96, 221) * mm, "end": v(871.62, 301.13) * mm, "construction": true});
            skLineSegment(sketch, "E319", {"start": v(776.49, 244.51) * mm, "end": v(796.31, 230.99) * mm, "construction": true});
            skLineSegment(sketch, "E320", {"start": v(774.8, 242.03) * mm, "end": v(794.62, 228.5) * mm, "construction": true});
            skLineSegment(sketch, "E321", {"start": v(776.49, 244.51) * mm, "end": v(774.8, 242.03) * mm, "construction": true});
            skLineSegment(sketch, "E322", {"start": v(794.62, 228.5) * mm, "end": v(796.31, 230.99) * mm, "construction": true});
            skLineSegment(sketch, "E323", {"start": v(658.17, 327.73) * mm, "end": v(712.83, 407.86) * mm, "construction": true});
            skLineSegment(sketch, "E324", {"start": v(712.83, 407.86) * mm, "end": v(751.65, 381.38) * mm, "construction": true});
            skLineSegment(sketch, "E325", {"start": v(751.65, 381.38) * mm, "end": v(697, 301.24) * mm, "construction": true});
            skLineSegment(sketch, "E326", {"start": v(697, 301.24) * mm, "end": v(658.17, 327.73) * mm, "construction": true});
            skPoint(sketch, "E327", {"position": v(677.58, 314.49) * mm});
            skLineSegment(sketch, "E328", {"start": v(721.15, 402.18) * mm, "end": v(743.45, 386.97) * mm, "construction": true});
            skLineSegment(sketch, "E329", {"start": v(721.15, 402.18) * mm, "end": v(729.6, 414.58) * mm, "construction": true});
            skLineSegment(sketch, "E330", {"start": v(729.6, 414.58) * mm, "end": v(751.9, 399.36) * mm, "construction": true});
            skLineSegment(sketch, "E331", {"start": v(751.9, 399.36) * mm, "end": v(743.45, 386.97) * mm, "construction": true});
            skPoint(sketch, "E332", {"position": v(732.3, 394.58) * mm});
            skLineSegment(sketch, "E333", {"start": v(637.81, 341.61) * mm, "end": v(756.26, 456.83) * mm, "construction": true});
            skLineSegment(sketch, "E334", {"start": v(871.62, 301.13) * mm, "end": v(889.8, 288.73) * mm, "construction": true});
            skLineSegment(sketch, "E335", {"start": v(840.38, 331.56) * mm, "end": v(879.2, 305.08) * mm, "construction": true});
            skLineSegment(sketch, "E336", {"start": v(653.86, 330.67) * mm, "end": v(701.3, 298.3) * mm, "construction": true});
            skLineSegment(sketch, "E337", {"start": v(780.27, 244.74) * mm, "end": v(945.35, 132.13) * mm});
            skPoint(sketch, "E338", {"position": v(868.06, 356.57) * mm});
            skLineSegment(sketch, "E339", {"start": v(727.04, 386.88) * mm, "end": v(703.9, 402.65) * mm, "construction": true});
            skCircle(sketch, "E340", {"center": v(695.83, 341.2) * mm, "radius": 1.5 * mm, "construction": true});
            skLineSegment(sketch, "E341", {"start": v(706.12, 380.2) * mm, "end": v(728.42, 364.96) * mm, "construction": true});
            skLineSegment(sketch, "E342", {"start": v(706.12, 380.2) * mm, "end": v(679.61, 341.39) * mm, "construction": true});
            skLineSegment(sketch, "E343", {"start": v(679.61, 341.39) * mm, "end": v(701.9, 326.15) * mm, "construction": true});
            skLineSegment(sketch, "E344", {"start": v(701.9, 326.15) * mm, "end": v(728.42, 364.96) * mm, "construction": true});
            skLineSegment(sketch, "E345", {"start": v(692.87, 360.8) * mm, "end": v(715.16, 345.56) * mm, "construction": true});
            skLineSegment(sketch, "E346", {"start": v(769.02, 448.32) * mm, "end": v(727.69, 476.56) * mm, "construction": true});
            skLineSegment(sketch, "E347", {"start": v(781.6, 439.55) * mm, "end": v(718.29, 286.72) * mm, "construction": true});
            skLineSegment(sketch, "E348", {"start": v(756.26, 456.83) * mm, "end": v(781.6, 439.55) * mm, "construction": true});
            skLineSegment(sketch, "E349", {"start": v(653.86, 330.67) * mm, "end": v(637.81, 341.61) * mm, "construction": true});
            skLineSegment(sketch, "E350", {"start": v(701.3, 298.3) * mm, "end": v(718.29, 286.72) * mm, "construction": true});
            skLineSegment(sketch, "E351", {"start": v(701.3, 298.3) * mm, "end": v(699.6, 295.83) * mm, "construction": true});
            skLineSegment(sketch, "E352", {"start": v(699.6, 295.83) * mm, "end": v(652.17, 328.2) * mm, "construction": true});
            skLineSegment(sketch, "E353", {"start": v(652.17, 328.2) * mm, "end": v(653.86, 330.67) * mm, "construction": true});
            skLineSegment(sketch, "E354", {"start": v(454.83, 576.68) * mm, "end": v(420.23, 416.55) * mm});
            skLineSegment(sketch, "E355", {"start": v(420.23, 416.55) * mm, "end": v(495.95, 416.55) * mm});
            skLineSegment(sketch, "E356", {"start": v(525.23, 416.55) * mm, "end": v(490.64, 576.68) * mm});
            skLineSegment(sketch, "E357", {"start": v(472.73, 416.55) * mm, "end": v(472.73, 592.22) * mm, "construction": true});
            skArc(sketch, "E358", {"start": v(454.83, 574.77) * mm, "mid": v(472.73, 556.87) * mm, "end": v(490.64, 574.77) * mm});
            skLineSegment(sketch, "E359.trimOffspring", {"start": v(495.95, 416.55) * mm, "end": v(525.23, 416.55) * mm});
            skCircle(sketch, "E360", {"center": v(472.73, 449.05) * mm, "radius": 1.5 * mm});
            skLineSegment(sketch, "E361", {"start": v(454.83, 574.77) * mm, "end": v(454.83, 576.68) * mm});
            skLineSegment(sketch, "E362", {"start": v(472.73, 574.77) * mm, "end": v(454.83, 574.77) * mm, "construction": true});
            skPoint(sketch, "E363.orphan", {"position": v(455.23, 578.55) * mm});
            skLineSegment(sketch, "E364", {"start": v(472.73, 574.77) * mm, "end": v(490.64, 574.77) * mm, "construction": true});
            skLineSegment(sketch, "E365", {"start": v(490.64, 574.77) * mm, "end": v(490.64, 576.68) * mm});
            skPoint(sketch, "E366.orphan", {"position": v(490.23, 578.55) * mm});
            skPoint(sketch, "E367.start.orphan", {"position": v(445.73, 416.55) * mm});
            const initialGuessF0  = {"E104": [0.7690192550415708, 0.4483164196433211, -0.5771491899465747, -0.8166387282905536, 0.01628397008579135, 0.015337817466823316, 4.737460054654662, 1.577010981135067]};
            skSetInitialGuess(sketch, initialGuessF0);
            skSolve(sketch);
        }
        {
            var Q0;
            Q0=makeQuery(id+"F0.imprint","IMPRINT",FACE,{"disambiguationData":[TD([[makeQuery(id+"F0.imprint","IMPRINT",EDGE,{"derivedFrom":sQuery(id+"F0.wireOp",EDGE,"E354")}),1.0]])]});
            extrude(context, id + "F1", {"entities" : qUnion([Q0]), "depth" : 3 * mm, "offsetDistance" : 25 * mm});
        }
        {
            var Q0;
            Q0=makeQuery(id+"F1.opExtrude","CAP_FACE",FACE,{"disambiguationData":[OSD([sQuery(id+"F0.wireOp",EDGE,"E354"),sQuery(id+"F0.wireOp",EDGE,"E355"),sQuery(id+"F0.wireOp",EDGE,"E356"),sQuery(id+"F0.wireOp",EDGE,"E358"),sQuery(id+"F0.wireOp",EDGE,"E359.trimOffspring"),sQuery(id+"F0.wireOp",EDGE,"E360"),sQuery(id+"F0.wireOp",EDGE,"E361"),sQuery(id+"F0.wireOp",EDGE,"E365")])],"isStart":false});
            var sketch = newSketch(context, id + "F2", { "sketchPlane" : qUnion([Q0])});
            skLineSegment(sketch, "E368.bottom", {"start": v(445.23, 416.55) * mm, "end": v(500.23, 416.55) * mm});
            skLineSegment(sketch, "E368.top", {"start": v(445.23, 413.55) * mm, "end": v(500.23, 413.55) * mm});
            skLineSegment(sketch, "E368.left", {"start": v(445.23, 416.55) * mm, "end": v(445.23, 413.55) * mm});
            skLineSegment(sketch, "E368.right", {"start": v(500.23, 416.55) * mm, "end": v(500.23, 413.55) * mm});
            skSolve(sketch);
        }
        {
            var Q0;
            Q0 = qSketchRegion(id + "F2", true);
            extrude(context, id + "F3", {"entities" : qUnion([Q0]), "operationType" : NewBodyOperationType.ADD, "oppositeDirection" : true, "depth" : 25 * mm, "offsetDistance" : 25 * mm});
        }
        {
            var Q0;
            {var subQ0=sQuery(id+"F0.wireOp",EDGE,"E359.trimOffspring");var subQ1=sQuery(id+"F0.wireOp",EDGE,"E355");Q0=makeQuery(id+"F3.boolean.opBoolean","SPLIT",EDGE,{"disambiguationData":[topologyDisambiguationEdgeConnected([makeQuery(id+"F1.opExtrude","CAP_FACE",FACE,{"disambiguationData":[OSD([sQuery(id+"F0.wireOp",EDGE,"E354"),subQ1,sQuery(id+"F0.wireOp",EDGE,"E356"),sQuery(id+"F0.wireOp",EDGE,"E358"),subQ0,sQuery(id+"F0.wireOp",EDGE,"E360"),sQuery(id+"F0.wireOp",EDGE,"E361"),sQuery(id+"F0.wireOp",EDGE,"E365")])],"isStart":true}),makeQuery(id+"F3.opExtrude","SWEPT_FACE",FACE,{"disambiguationData":[OSD([sQuery(id+"F2.wireOp",EDGE,"E368.bottom")])]})])],"derivedFrom":makeQuery(id+"F1.opExtrude","CAP_EDGE",EDGE,{"disambiguationData":[OSD([subQ1,subQ0])],"isStart":true})});}
            var Q1;
            Q1=makeQuery(id+"F3.opExtrude","CAP_EDGE",EDGE,{"disambiguationData":[OSD([sQuery(id+"F2.wireOp",EDGE,"E368.top")])],"isStart":true});
            fillet(context, id + "F4", {"entities" : qUnion([Q0, Q1]), "radius" : 3 * mm, "tangentPropagation" : true, "allowEdgeOverflow" : false});
        }
        {
            var Q0;
            Q0=makeQuery(id+"F3.opExtrude","SWEPT_FACE",FACE,{"disambiguationData":[OSD([sQuery(id+"F2.wireOp",EDGE,"E368.top")])]});
            var sketch = newSketch(context, id + "F5", { "sketchPlane" : qUnion([Q0])});
            skCircle(sketch, "E369", {"center": v(472.73, -6.5) * mm, "radius": 3 * mm});
            skPoint(sketch, "E369.centerSnap0", {"position": v(472.73, 0) * mm});
            skSolve(sketch);
        }
        {
            var Q0;
            Q0 = qSketchRegion(id + "F5", true);
            extrude(context, id + "F6", {"entities" : qUnion([Q0]), "operationType" : NewBodyOperationType.REMOVE, "endBound" : BoundingType.THROUGH_ALL, "oppositeDirection" : true, "depth" : 25 * mm, "offsetDistance" : 25 * mm});
        }
    });
